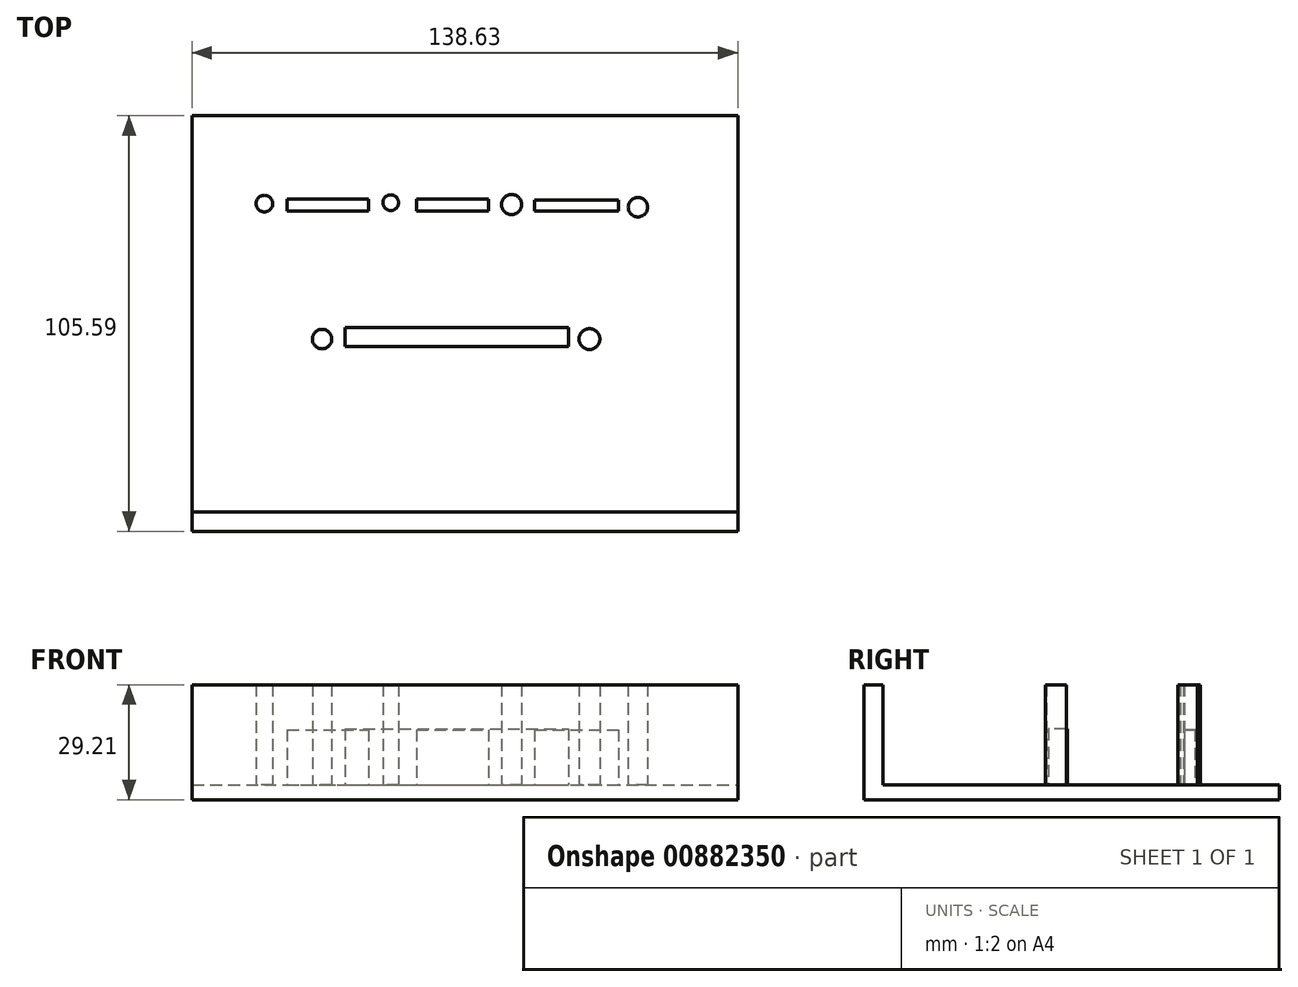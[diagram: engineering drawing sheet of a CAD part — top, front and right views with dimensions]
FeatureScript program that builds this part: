
annotation { "Feature Type Name" : "Feature", "Feature Type Description" : "" }
export const myFeature = defineFeature(function(context is Context, id is Id, definition is map)
    precondition{}
    {
        {
            var Q0;
            Q0=qCreatedBy(makeId("Top.planeOp"),FACE);
            var sketch = newSketch(context, id + "F0", { "sketchPlane" : qUnion([Q0])});
            skLineSegment(sketch, "E0.bottom", {"start": v(-67.57, 53.84) * mm, "end": v(71.06, 53.84) * mm});
            skLineSegment(sketch, "E0.top", {"start": v(-67.57, -51.75) * mm, "end": v(71.06, -51.75) * mm});
            skLineSegment(sketch, "E0.left", {"start": v(-67.57, 53.84) * mm, "end": v(-67.57, -51.75) * mm});
            skLineSegment(sketch, "E0.right", {"start": v(71.06, 53.84) * mm, "end": v(71.06, -51.75) * mm});
            skSolve(sketch);
        }
        {
            var Q0;
            Q0 = qSketchRegion(id + "F0", true);
            extrude(context, id + "F1", {"entities" : qUnion([Q0]), "depth" : 3.8 * mm, "offsetDistance" : 25.4 * mm});
        }
        {
            var Q0;
            Q0=makeQuery(id+"F1.opExtrude","CAP_FACE",FACE,{"disambiguationData":[OSD([sQuery(id+"F0.wireOp",EDGE,"E0.bottom"),sQuery(id+"F0.wireOp",EDGE,"E0.top"),sQuery(id+"F0.wireOp",EDGE,"E0.left"),sQuery(id+"F0.wireOp",EDGE,"E0.right")])],"isStart":false});
            var sketch = newSketch(context, id + "F2", { "sketchPlane" : qUnion([Q0])});
            skCircle(sketch, "E1", {"center": v(-49.2, 31.52) * mm, "radius": 2.1 * mm});
            skSolve(sketch);
        }
        {
            var Q0;
            Q0 = qSketchRegion(id + "F2", true);
            extrude(context, id + "F3", {"entities" : qUnion([Q0]), "operationType" : NewBodyOperationType.ADD, "depth" : 25.4 * mm, "offsetDistance" : 25.4 * mm});
        }
        {
            var Q0;
            Q0=makeQuery(id+"F1.opExtrude","CAP_FACE",FACE,{"disambiguationData":[OSD([sQuery(id+"F0.wireOp",EDGE,"E0.bottom"),sQuery(id+"F0.wireOp",EDGE,"E0.top"),sQuery(id+"F0.wireOp",EDGE,"E0.left"),sQuery(id+"F0.wireOp",EDGE,"E0.right")])],"isStart":false});
            var sketch = newSketch(context, id + "F4", { "sketchPlane" : qUnion([Q0])});
            skCircle(sketch, "E2", {"center": v(-17.1, 31.75) * mm, "radius": 2 * mm});
            skSolve(sketch);
        }
        {
            var Q0;
            Q0 = qSketchRegion(id + "F4", true);
            extrude(context, id + "F5", {"entities" : qUnion([Q0]), "operationType" : NewBodyOperationType.ADD, "depth" : 25.4 * mm, "offsetDistance" : 25.4 * mm});
        }
        {
            var Q0;
            Q0=makeQuery(id+"F1.opExtrude","CAP_FACE",FACE,{"disambiguationData":[OSD([sQuery(id+"F0.wireOp",EDGE,"E0.bottom"),sQuery(id+"F0.wireOp",EDGE,"E0.top"),sQuery(id+"F0.wireOp",EDGE,"E0.left"),sQuery(id+"F0.wireOp",EDGE,"E0.right")])],"isStart":false});
            var sketch = newSketch(context, id + "F6", { "sketchPlane" : qUnion([Q0])});
            skCircle(sketch, "E3", {"center": v(13.6, 31.28) * mm, "radius": 2.56 * mm});
            skSolve(sketch);
        }
        {
            var Q0;
            Q0 = qSketchRegion(id + "F6", true);
            extrude(context, id + "F7", {"entities" : qUnion([Q0]), "operationType" : NewBodyOperationType.ADD, "depth" : 25.4 * mm, "offsetDistance" : 25.4 * mm});
        }
        {
            var Q0;
            Q0=makeQuery(id+"F1.opExtrude","CAP_FACE",FACE,{"disambiguationData":[OSD([sQuery(id+"F0.wireOp",EDGE,"E0.bottom"),sQuery(id+"F0.wireOp",EDGE,"E0.top"),sQuery(id+"F0.wireOp",EDGE,"E0.left"),sQuery(id+"F0.wireOp",EDGE,"E0.right")])],"isStart":false});
            var sketch = newSketch(context, id + "F8", { "sketchPlane" : qUnion([Q0])});
            skCircle(sketch, "E4", {"center": v(45.7, 30.59) * mm, "radius": 2.47 * mm});
            skSolve(sketch);
        }
        {
            var Q0;
            Q0 = qSketchRegion(id + "F8", true);
            extrude(context, id + "F9", {"entities" : qUnion([Q0]), "operationType" : NewBodyOperationType.ADD, "depth" : 25.4 * mm, "offsetDistance" : 25.4 * mm});
        }
        {
            var Q0;
            Q0=makeQuery(id+"F1.opExtrude","CAP_FACE",FACE,{"disambiguationData":[OSD([sQuery(id+"F0.wireOp",EDGE,"E0.bottom"),sQuery(id+"F0.wireOp",EDGE,"E0.top"),sQuery(id+"F0.wireOp",EDGE,"E0.left"),sQuery(id+"F0.wireOp",EDGE,"E0.right")])],"isStart":false});
            var sketch = newSketch(context, id + "F10", { "sketchPlane" : qUnion([Q0])});
            skLineSegment(sketch, "E5.bottom", {"start": v(-67.57, -46.87) * mm, "end": v(71.06, -46.87) * mm});
            skLineSegment(sketch, "E5.top", {"start": v(-67.57, -51.75) * mm, "end": v(71.06, -51.75) * mm});
            skLineSegment(sketch, "E5.left", {"start": v(-67.57, -46.87) * mm, "end": v(-67.57, -51.75) * mm});
            skLineSegment(sketch, "E5.right", {"start": v(71.06, -46.87) * mm, "end": v(71.06, -51.75) * mm});
            skSolve(sketch);
        }
        {
            var Q0;
            Q0 = qSketchRegion(id + "F10", true);
            extrude(context, id + "F11", {"entities" : qUnion([Q0]), "operationType" : NewBodyOperationType.ADD, "depth" : 25.4 * mm, "offsetDistance" : 25.4 * mm});
        }
        {
            var Q0;
            Q0=makeQuery(id+"F1.opExtrude","CAP_FACE",FACE,{"disambiguationData":[OSD([sQuery(id+"F0.wireOp",EDGE,"E0.bottom"),sQuery(id+"F0.wireOp",EDGE,"E0.top"),sQuery(id+"F0.wireOp",EDGE,"E0.left"),sQuery(id+"F0.wireOp",EDGE,"E0.right")])],"isStart":false});
            var sketch = newSketch(context, id + "F12", { "sketchPlane" : qUnion([Q0])});
            skCircle(sketch, "E6", {"center": v(-34.54, -2.9) * mm, "radius": 2.47 * mm});
            skSolve(sketch);
        }
        {
            var Q0;
            Q0 = qSketchRegion(id + "F12", true);
            extrude(context, id + "F13", {"entities" : qUnion([Q0]), "operationType" : NewBodyOperationType.ADD, "depth" : 25.4 * mm, "offsetDistance" : 25.4 * mm});
        }
        {
            var Q0;
            Q0=makeQuery(id+"F1.opExtrude","CAP_FACE",FACE,{"disambiguationData":[OSD([sQuery(id+"F0.wireOp",EDGE,"E0.bottom"),sQuery(id+"F0.wireOp",EDGE,"E0.top"),sQuery(id+"F0.wireOp",EDGE,"E0.left"),sQuery(id+"F0.wireOp",EDGE,"E0.right")])],"isStart":false});
            var sketch = newSketch(context, id + "F14", { "sketchPlane" : qUnion([Q0])});
            skCircle(sketch, "E7", {"center": v(33.38, -2.9) * mm, "radius": 2.65 * mm});
            skSolve(sketch);
        }
        {
            var Q0;
            Q0 = qSketchRegion(id + "F14", true);
            extrude(context, id + "F15", {"entities" : qUnion([Q0]), "operationType" : NewBodyOperationType.ADD, "depth" : 25.4 * mm, "offsetDistance" : 25.4 * mm});
        }
        {
            var Q0;
            Q0=makeQuery(id+"F1.opExtrude","CAP_FACE",FACE,{"disambiguationData":[OSD([sQuery(id+"F0.wireOp",EDGE,"E0.bottom"),sQuery(id+"F0.wireOp",EDGE,"E0.top"),sQuery(id+"F0.wireOp",EDGE,"E0.left"),sQuery(id+"F0.wireOp",EDGE,"E0.right")])],"isStart":false});
            var sketch = newSketch(context, id + "F16", { "sketchPlane" : qUnion([Q0])});
            skLineSegment(sketch, "E8.bottom", {"start": v(-43.38, 32.68) * mm, "end": v(-22.68, 32.68) * mm});
            skLineSegment(sketch, "E8.top", {"start": v(-43.38, 29.65) * mm, "end": v(-22.68, 29.65) * mm});
            skLineSegment(sketch, "E8.left", {"start": v(-43.38, 32.68) * mm, "end": v(-43.38, 29.65) * mm});
            skLineSegment(sketch, "E8.right", {"start": v(-22.68, 32.68) * mm, "end": v(-22.68, 29.65) * mm});
            skPoint(sketch, "E9.firstSnap0", {"position": v(-33.03, 32.68) * mm});
            skLineSegment(sketch, "E9.bottom", {"start": v(-10.58, 32.68) * mm, "end": v(7.8, 32.68) * mm});
            skLineSegment(sketch, "E9.top", {"start": v(-10.58, 29.65) * mm, "end": v(7.8, 29.65) * mm});
            skLineSegment(sketch, "E9.left", {"start": v(-10.58, 32.68) * mm, "end": v(-10.58, 29.65) * mm});
            skLineSegment(sketch, "E9.right", {"start": v(7.8, 32.68) * mm, "end": v(7.8, 29.65) * mm});
            skLineSegment(sketch, "E10.bottom", {"start": v(19.42, 29.65) * mm, "end": v(40.82, 29.65) * mm});
            skLineSegment(sketch, "E10.top", {"start": v(19.42, 32.45) * mm, "end": v(40.82, 32.45) * mm});
            skLineSegment(sketch, "E10.left", {"start": v(19.42, 29.65) * mm, "end": v(19.42, 32.45) * mm});
            skLineSegment(sketch, "E10.right", {"start": v(40.82, 29.65) * mm, "end": v(40.82, 32.45) * mm});
            skSolve(sketch);
        }
        {
            var Q0;
            Q0 = qSketchRegion(id + "F16", true);
            extrude(context, id + "F17", {"entities" : qUnion([Q0]), "operationType" : NewBodyOperationType.ADD, "depth" : 13.97 * mm, "offsetDistance" : 25.4 * mm});
        }
        {
            var Q0;
            Q0=makeQuery(id+"F1.opExtrude","CAP_FACE",FACE,{"disambiguationData":[OSD([sQuery(id+"F0.wireOp",EDGE,"E0.bottom"),sQuery(id+"F0.wireOp",EDGE,"E0.top"),sQuery(id+"F0.wireOp",EDGE,"E0.left"),sQuery(id+"F0.wireOp",EDGE,"E0.right")])],"isStart":false});
            var sketch = newSketch(context, id + "F18", { "sketchPlane" : qUnion([Q0])});
            skLineSegment(sketch, "E11.bottom", {"start": v(-28.72, 0) * mm, "end": v(28.03, 0) * mm});
            skLineSegment(sketch, "E11.top", {"start": v(-28.72, -4.77) * mm, "end": v(28.03, -4.77) * mm});
            skLineSegment(sketch, "E11.left", {"start": v(-28.72, 0) * mm, "end": v(-28.72, -4.77) * mm});
            skLineSegment(sketch, "E11.right", {"start": v(28.03, 0) * mm, "end": v(28.03, -4.77) * mm});
            skSolve(sketch);
        }
        {
            var Q0;
            Q0 = qSketchRegion(id + "F18", true);
            extrude(context, id + "F19", {"entities" : qUnion([Q0]), "operationType" : NewBodyOperationType.ADD, "depth" : 14.22 * mm, "offsetDistance" : 25.4 * mm});
        }
    });
